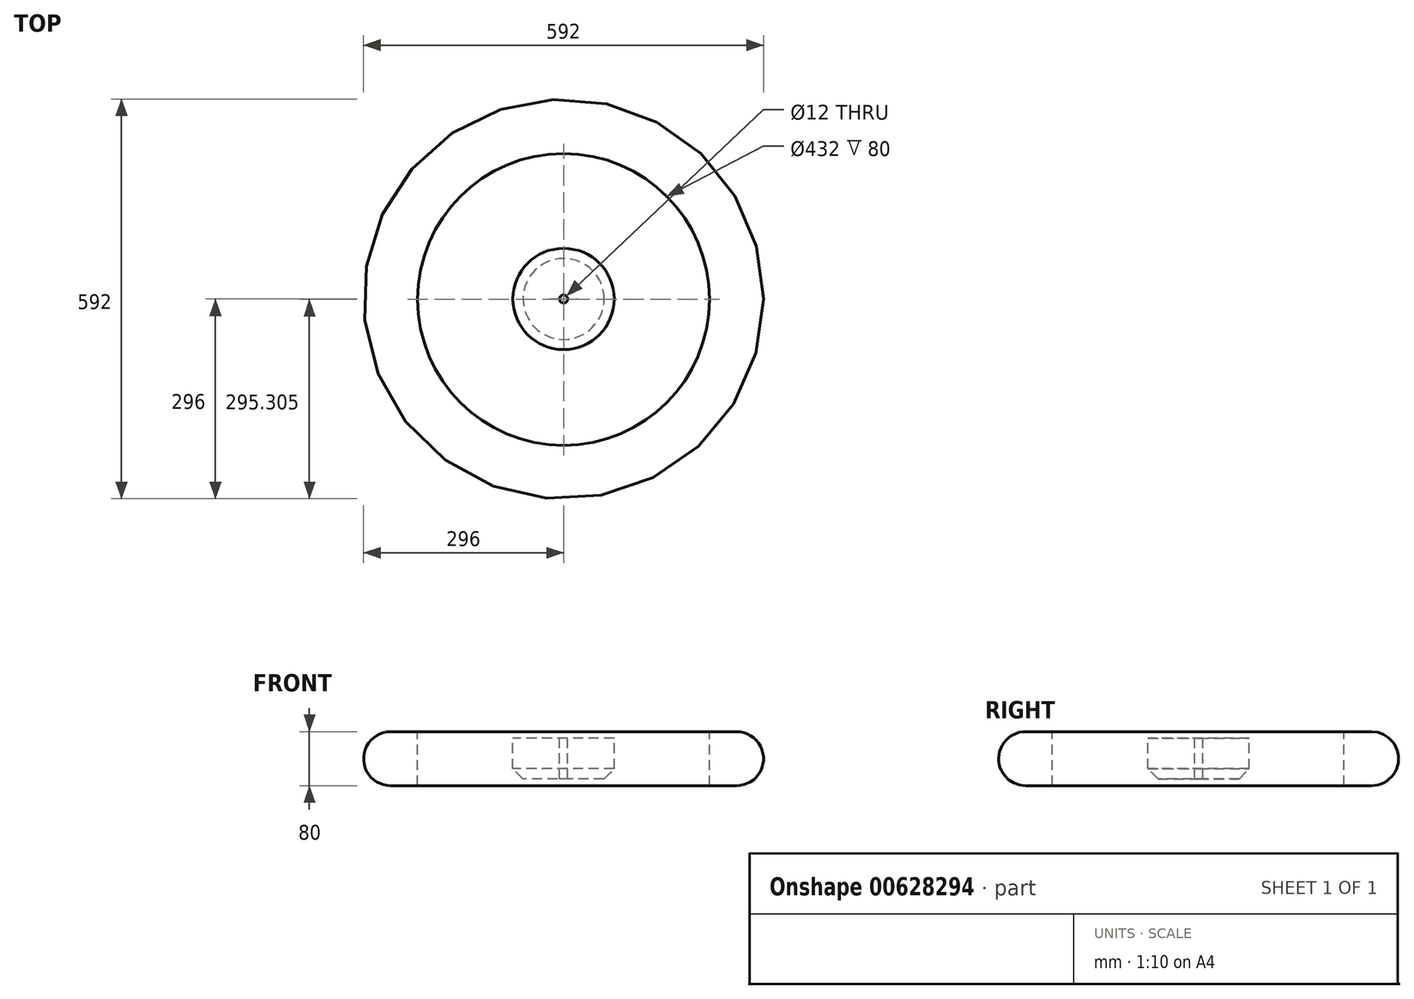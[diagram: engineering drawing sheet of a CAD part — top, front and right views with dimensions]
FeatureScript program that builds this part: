
annotation { "Feature Type Name" : "Feature", "Feature Type Description" : "" }
export const myFeature = defineFeature(function(context is Context, id is Id, definition is map)
    precondition{}
    {
        {
            var Q0;
            Q0=qCreatedBy(makeId("Top.planeOp"),FACE);
            var sketch = newSketch(context, id + "F0", { "sketchPlane" : qUnion([Q0])});
            skCircle(sketch, "E0", {"center": v(0, -0.7) * mm, "radius": 216 * mm});
            skCircle(sketch, "E1", {"center": v(0, 0) * mm, "radius": 296 * mm});
            skCircle(sketch, "E2", {"center": v(0, 0) * mm, "radius": 75 * mm});
            skCircle(sketch, "E3", {"center": v(0, 0) * mm, "radius": 6 * mm});
            skSolve(sketch);
        }
        {
            var Q0;
            Q0=makeQuery(id+"F0.imprint","IMPRINT",FACE,{"disambiguationData":[TD([[makeQuery(id+"F0.imprint","IMPRINT",EDGE,{"derivedFrom":sQuery(id+"F0.wireOp",EDGE,"E0")}),-1.0]])]});
            extrude(context, id + "F1", {"entities" : qUnion([Q0]), "oppositeDirection" : true, "depth" : 80 * mm, "offsetDistance" : 25 * mm});
        }
        {
            var Q0;
            Q0=makeQuery(id+"F1.opExtrude","CAP_EDGE",EDGE,{"disambiguationData":[OSD([sQuery(id+"F0.wireOp",EDGE,"E1")])],"isStart":true});
            var Q1;
            Q1=makeQuery(id+"F1.opExtrude","CAP_EDGE",EDGE,{"disambiguationData":[OSD([sQuery(id+"F0.wireOp",EDGE,"E1")])],"isStart":false});
            fillet(context, id + "F2", {"entities" : qUnion([Q0, Q1]), "radius" : 40 * mm, "tangentPropagation" : true, "allowEdgeOverflow" : false});
        }
        {
            var Q0;
            Q0=makeQuery(id+"F0.imprint","IMPRINT",FACE,{"disambiguationData":[TD([[makeQuery(id+"F0.imprint","IMPRINT",EDGE,{"derivedFrom":sQuery(id+"F0.wireOp",EDGE,"E2")}),1.0]])]});
            extrude(context, id + "F3", {"entities" : qUnion([Q0]), "oppositeDirection" : true, "depth" : 70 * mm, "offsetDistance" : 25 * mm});
        }
        {
            var Q0;
            Q0=makeQuery(id+"F3.opExtrude","CAP_FACE",FACE,{"disambiguationData":[OSD([sQuery(id+"F0.wireOp",EDGE,"E2"),sQuery(id+"F0.wireOp",EDGE,"E3")])],"isStart":true});
            extrude(context, id + "F4", {"entities" : qUnion([Q0]), "operationType" : NewBodyOperationType.REMOVE, "oppositeDirection" : true, "depth" : 10 * mm, "offsetDistance" : 25 * mm});
        }
        {
            var Q0;
            Q0=makeQuery(id+"F4.boolean.opBoolean","COPY",EDGE,{"derivedFrom":makeQuery(id+"F4.opExtrude","CAP_EDGE",EDGE,{"disambiguationData":[OSD([sQuery(id+"F0.wireOp",EDGE,"E2")])],"isStart":false})});
            var Q1;
            Q1=makeQuery(id+"F3.opExtrude","CAP_EDGE",EDGE,{"disambiguationData":[OSD([sQuery(id+"F0.wireOp",EDGE,"E2")])],"isStart":false});
            chamfer(context, id + "F5", {"entities" : qUnion([Q0, Q1]), "width" : 15 * mm, "tangentPropagation" : true});
        }
    });
